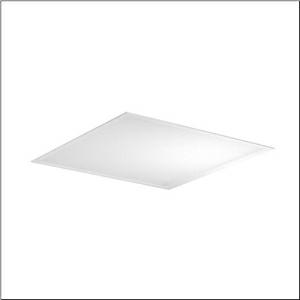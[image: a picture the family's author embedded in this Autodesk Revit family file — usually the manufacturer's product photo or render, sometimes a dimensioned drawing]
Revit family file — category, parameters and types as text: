
# Revit family: apollon_21_square_51mq12wd2114
name_source: partatom
category: Lighting Fixtures
units: mm (PartAtom-declared; Revit-internal decimal feet)

## family parameters
Cut with Voids When Loaded = No
Host = Face
Light Source = No
Part Type = Normal
Room Calculation Point = No
Round Connector Dimension = Use Diameter
Shared = No

## types (1)
- Apollon 21 square (1 x LED, 4100 lm, 24.7 W, 4000K)
    Apparent Load = 25 VA
    CIE Flux Codes = 60 87 97 100 100
    Color Rendering = 90
    Color Temperature = 4000K
    Default Elevation = 1800 mm
    Description = Apollon 21 square, office luminaire, primary optical cover: micro prismatic cover, of PMMA, CAT 2 (L<= 3000cd/m²), light emission: direct distribution, primary light characteristic: symmetric, installation type: lay-in mounting, recessed, LED, rated luminous flux: 4.100lm, luminous efficacy: 166lm/W, light colour: 940, colour temperature: 4000K, control gear: DALI 2, Multilumen, with terminal, 5-pole, mains connection: 220..240V, AC/DC, 0/50..60Hz, rated input power: 24.7W, suitable for self-contained emergency lighting element 59MQE002602A with integrated self-test function according to EN 60598-2-22, housing, of aluminium, coated, traffic white (RAL 9016), module: M600, length: 595mm, width: 595mm, height: 55mm, housing upper side, of sheet steel, galvanised, protection rating (complete): IP20, protection rating (lamp compartment, on room side): IP50, insulation class (complete): insulation class II (safety insulation), certification: CE, ENEC, UKCA, impact resistance: IK03, permissible operating ambient temperature: -20..+45°C, standard: EN 60598-2-22, corresponds to IFS (International Featured Standards) requirements for safety and quality in the food industry, packaging unit: 1 piece
    Height = 0 mm  [stored 0 ft]
    Lamp = 1 x LED
    Lamp Light Flux = 4100 lm
    Lamp Power = 24.7 W
    Lamp count = 1
    Length = 595 mm
    Luminous efficacy = 166 lm/W
    Manufacturer = Siteco
    ModVariant = No
    Model = 51MQ12WD2114
    Mounting Place = Ceiling
    Mounting Type = Recessed
    Number of Poles = 1
    OnlyDefault = Yes
    Power Factor = 1
    Product Name = Apollon 21 square
    Product group = office luminaire | ceiling recessed
    ProductGroupID = 400
    Protection Class = Protection class II
    Protection Degree = IP 20
    RLX_Detail_Level = 1
    RLX_Emergency_Light_Flux = 0 lm
    RLX_Emergency_Type = 0
    RLX_Emergency_Type_DB = No
    RlxData = <blob elided: 97173 chars, md5=677c52df>
    Socket = socket
    Standby Power = 0 W
    System Light Flux = 4100 lm
    System Power = 25 W
    Type Comments = Product without accessories
    Type Image = l_1291049.jpg
    URL = http://relux.com
    VarID = ---
    Voltage = 0 V
    Weight = 0.00 kg
    Width = 595 mm

note: [stored X ft] marks values corroborated as IEEE doubles in the binary element streams (Revit-internal decimal feet)

## geometry (parser evidence)
native form markers: Blend x4, Sweep x12
no freeform markers — native parametric forms only
